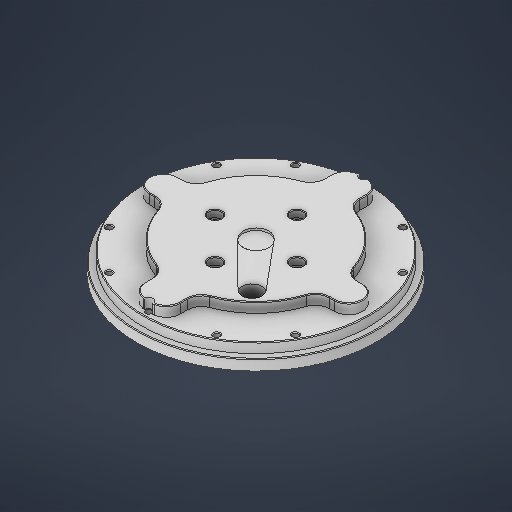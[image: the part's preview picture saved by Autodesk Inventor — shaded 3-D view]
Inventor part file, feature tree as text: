
AUTODESK INVENTOR PART (.ipt)
format: ipt  version: 2025 (Build 290162000, 162)  size: 554,496 bytes
history: native  units: in
note: dims shown in document units (in); Inventor stores cm internally (conversion verified against a paired STEP export)
features: sketch x14, extrude x9, hole x4, chamfer x3
ambient origin geometry x8: Origin, YZ Plane, XZ Plane, XY Plane, X Axis, Y Axis, Z Axis, Center Point
bodies: Solid1 (feature_tree)
feature tree (30):
  sketch  "Sketch1"  dims[d3=4.3307in d24=6.6535in]
  extrude  "Extrusion1"  Depth=6.6535in
  extrude  "Extrusion2"  Depth=5.9843in
  extrude  "Extrusion3"  Depth=4.3307in
  sketch  "Sketch2"  dims[d27=0.9843in d28=4.3307in]
  extrude  "Extrusion4"  Depth=0.3937in
  hole  "Hole1"  [1 undecoded]
  hole  "Hole2"  [1 undecoded]
  sketch  "Sketch4"  dims[d38=0.2953in d39=0.0in d40=2.2835in]
  extrude  "Extrusion5"  Depth=2.2835in
  extrude  "Extrusion6"  Depth=0.1969in
  hole  "Hole3"  [1 undecoded]
  chamfer  "Chamfer1"  Distance=0.7874in Angle=360.0deg
  chamfer  "Chamfer2"  Distance=0.1969in
  hole  "Hole5"  [1 undecoded]
  extrude  "Extrusion9"  Depth=0.0591in TaperAngle=0.0deg
  extrude  "Extrusion10"  Depth=0.0197in TaperAngle=0.0deg
  chamfer  "Chamfer4"  Distance=0.1969in
  extrude  "Extrusion11"  Depth=0.0197in TaperAngle=360.0deg
  sketch  "Sketch Circular Pattern1"  dims[d25=6.2992in d26=5.9843in]
  sketch  "Sketch3"  dims[d31=0.3937in d32=0.3937in]
  sketch  "Sketch Circular Pattern2"  dims[d29=0.7874in d30=0.3937in]
  sketch  "Sketch5"  dims[d41=0.3543in d42=0.1969in]
  sketch  "Sketch Circular Pattern3"  dims[d34=0.8465in d35=0.0in d36=0.5709in d37=0.0in]
  sketch  "Sketch7"  dims[d56=5.9843in]
  sketch  "Sketch Circular Pattern5"  dims[d43=1.5748in d45=360.0deg d47=0.1969in d48=0.0in]
  sketch  "Sketch9"  dims[d57=0.1378in d58=0.7874in d60=360.0deg]
  sketch  "Sketch Circular Pattern6"  dims[d49=0.2165in d50=0.7874in d51=0.1575in d52=0.0787in d53=90.0deg d54=0.315in d55=0.8108in]
  sketch  "Sketch10"  dims[d62=0.1628in d63=0.3937in d64=0.2362in d65=0.2756in d66=90.0deg d67=0.4646in d68=0.0in]
  sketch  "Sketch11"  dims[d69=3.2283in d70=0.1969in d71=0.7874in d72=0.0591in d73=0.0in d74=0.4724in d75=0.0in d76=0.1969in d77=4.7244in d79=360.0deg d81=0.1628in d82=0.7874in d83=0.1575in d84=0.0787in d85=90.0deg d86=0.3937in d87=0.8108in d88=0.0197in d89=0.0787in d90=45.0deg d91=0.0197in d92=0.0787in d93=45.0deg d107=3.7402in d108=0.1969in d109=6.2992in d111=360.0deg d113=0.1969in d114=0.7874in d115=0.748in d116=0.3543in d117=90.0deg d118=0.7874in d119=0.8108in d139=0.7185in d140=3.1496in d141=0.7185in d142=3.1496in d144=360.0deg d146=0.0591in d147=0.0in d151=0.5512in d152=1.7717in d153=0.0in d154=0.0in d155=0.0197in d156=0.0787in d157=45.0deg d158=0.5512in d159=1.7717in d160=0.0394in d161=0.0in d162=0.1969in d137=0.0197in d138=0.0344in]
note: 4 required parameter values undecoded (feature->parameter linkage not recoverable at this tier; creation-order binding heuristic only, values carry confidence <= 0.55)
